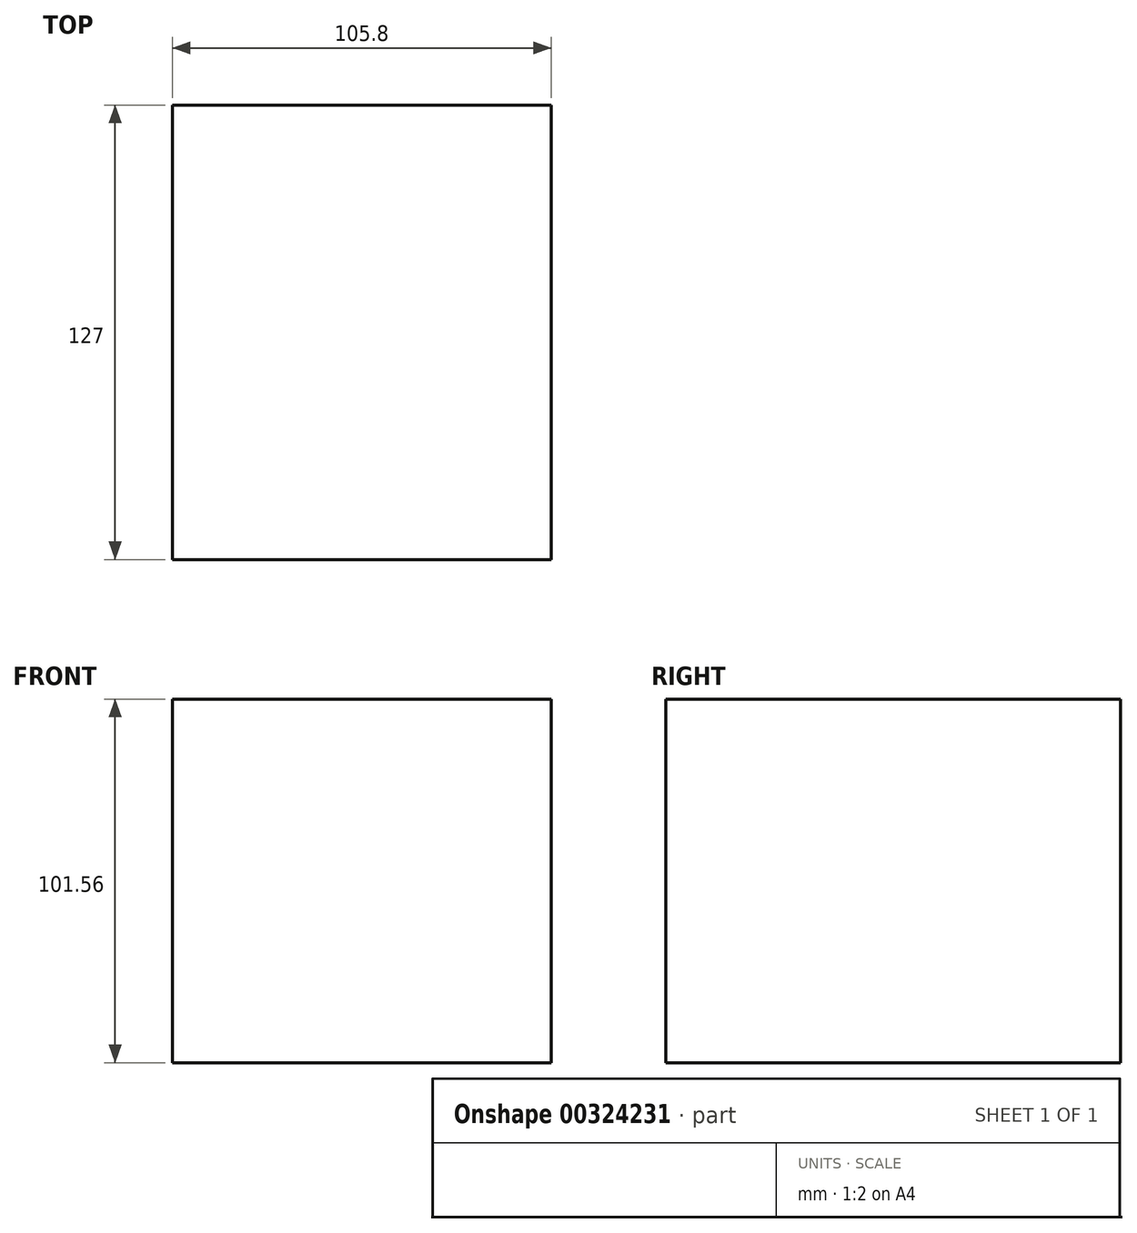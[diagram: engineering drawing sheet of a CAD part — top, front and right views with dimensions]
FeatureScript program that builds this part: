
annotation { "Feature Type Name" : "Feature", "Feature Type Description" : "" }
export const myFeature = defineFeature(function(context is Context, id is Id, definition is map)
    precondition{}
    {
        {
            var Q0;
            Q0=qCreatedBy(makeId("Front.planeOp"),FACE);
            var sketch = newSketch(context, id + "F0", { "sketchPlane" : qUnion([Q0])});
            skLineSegment(sketch, "E0.bottom", {"start": v(52.9, 50.78) * mm, "end": v(-52.9, 50.78) * mm});
            skLineSegment(sketch, "E0.top", {"start": v(52.9, -50.78) * mm, "end": v(-52.9, -50.78) * mm});
            skLineSegment(sketch, "E0.left", {"start": v(52.9, 50.78) * mm, "end": v(52.9, -50.78) * mm});
            skLineSegment(sketch, "E0.right", {"start": v(-52.9, 50.78) * mm, "end": v(-52.9, -50.78) * mm});
            skPoint(sketch, "E0.middle", {"position": v(0, 0) * mm});
            skSolve(sketch);
        }
        {
            var Q0;
            Q0=makeQuery(id+"F0.imprint","IMPRINT",FACE,{"disambiguationData":[TD([[makeQuery(id+"F0.imprint","IMPRINT",EDGE,{"derivedFrom":sQuery(id+"F0.wireOp",EDGE,"E0.bottom")}),1.0]])]});
            extrude(context, id + "F1", {"entities" : qUnion([Q0]), "endBound" : BoundingType.SYMMETRIC, "depth" : 127 * mm});
        }
    });
